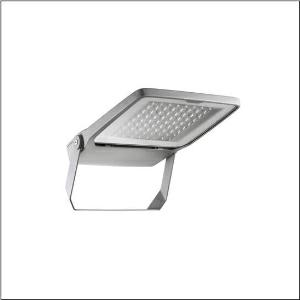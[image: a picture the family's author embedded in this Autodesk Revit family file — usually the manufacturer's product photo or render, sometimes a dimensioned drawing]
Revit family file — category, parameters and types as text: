
# Revit family: floodlight_fl_20_mini___pl61_5xa7672b2c1ac_8a65
name_source: partatom
category: Lighting Fixtures
units: mm (PartAtom-declared; Revit-internal decimal feet)

## family parameters
Cut with Voids When Loaded = No
Host = Face
Light Source = No
Part Type = Normal
Room Calculation Point = No
Round Connector Dimension = Use Diameter
Shared = No

## types (1)
- --- (1 x LED 4000K / CRI = 70 (unbekannt), 6350 lm, 4000K)
    Apparent Load = 51 VA
    CIE Flux Codes = 33 65 98 100 100
    Color Rendering = 70
    Color Temperature = 4000K
    Default Elevation = 1800 mm
    Description = Floodlight FL 20 mini, floodlight, primary light control with lens, of plastic, primary optical cover: protective disc, of toughened safety glass, transparent, light distribution: PL61, light emission: direct distribution, primary light characteristic: asymmetric, installation type: surface-mounted, LED, High Power LED, rated luminous flux: 6.350lm, luminous efficacy: 125lm/W, light colour: 740, colour temperature: 4000K, control gear: ECG Plus, control: flexible luminous flux parameterisation, time-dependent luminous flux control, digital communication interface, power reduction, overheat protection, electronic power reduction, with terminal, 5-pole, max. 2.5mm², mains connection: 220..240V, AC, 50/60Hz, rated input power: 51W, LED unit, of diecast aluminium, powder-coated, Siteco® metallic grey (DB 702S), corrosivity category C5 mid according to DIN EN ISO 12944, incl. 1x M20 cable gland for cable Ø 6.5..12mm, length: 446mm, width: 355mm, height: 62mm, housing frame, of diecast aluminium, powder-coated, Siteco® metallic grey (DB 702S), mounting bracket, of steel, powder-coated, Siteco® metallic grey (DB 702S), DALI, protection rating (complete): IP66, insulation class (complete): insulation class II (safety insulation), certification: CE, ENEC, VDE, protection symbol: D, permissible operating ambient temperature: -40..+40°C, permissible operating ambient temperature for outdoor applications: -40..+50°C, standard: DIN EN 12944, packaging unit: 1 piece

Light Distribution: PL61
    Height = 62 mm  [stored 0.203412 ft]
    Lamp = 1 x LED 4000K / CRI >= 70 (unbekannt)
    Lamp Light Flux = 6350 lm
    Lamp count = 1
    Length = 467 mm
    Luminous efficacy = 125 lm/W
    Manufacturer = Siteco
    ModVariant = No
    Model = 5XA7672B2C1AC
    Mounting Place = Wall
    Mounting Type = Surface mounted
    Number of Poles = 1
    OnlyDefault = Yes
    Power Factor = 1
    Product Name = Floodlight FL 20 mini | PL61
    Product group = floodlight | wall mounted
    ProductGroupID = 2001
    Protection Class = Protection class II
    Protection Degree = IP 66
    RLX_Detail_Level = 1
    RLX_Emergency_Light_Flux = 0 lm
    RLX_Emergency_Type = 0
    RLX_Emergency_Type_DB = No
    RlxData = <blob elided: 74325 chars, md5=d0f44ab6>
    Socket = socket
    Standby Power = 0 W
    System Light Flux = 6350 lm
    System Power = 51 W
    Type Comments = factory setting: luminous flux: 100 % | dim-lin: 254 | 520 mA
    Type Image = l_1005948.jpg
    URL = http://relux.com
    VarID = @adj_163521
    Voltage = 0 V
    Weight = 0.00 kg
    Width = 335 mm

note: [stored X ft] marks values corroborated as IEEE doubles in the binary element streams (Revit-internal decimal feet)

## geometry (parser evidence)
native form markers: Blend x4, Sweep x14
no freeform markers — native parametric forms only
